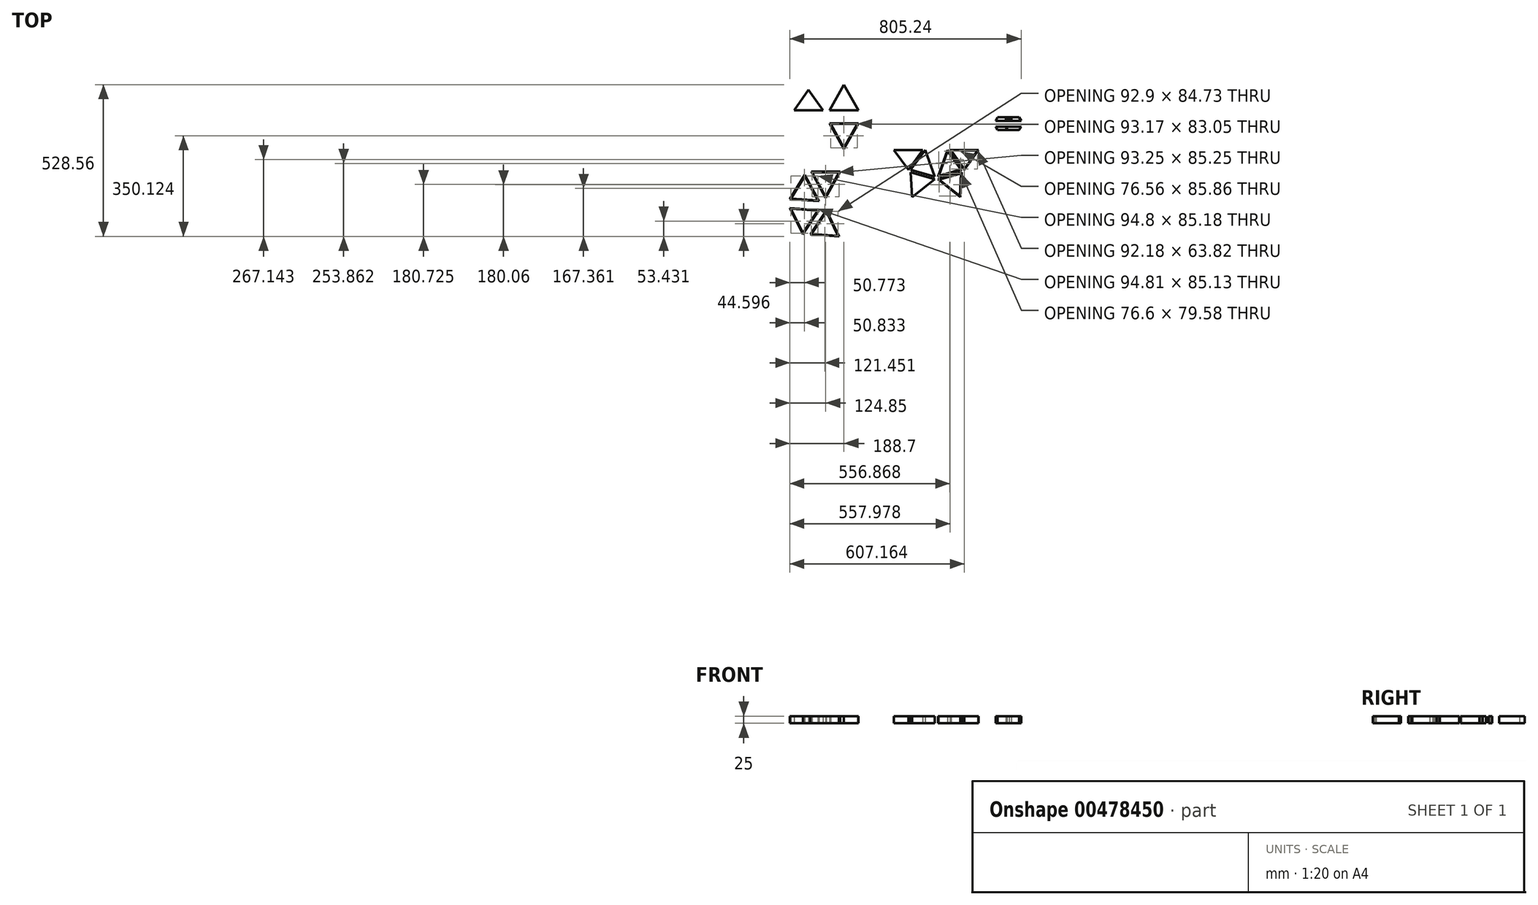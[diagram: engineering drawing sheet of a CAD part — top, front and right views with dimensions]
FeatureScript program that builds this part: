
annotation { "Feature Type Name" : "Feature", "Feature Type Description" : "" }
export const myFeature = defineFeature(function(context is Context, id is Id, definition is map)
    precondition{}
    {
        {
            var Q0;
            Q0=qCreatedBy(makeId("Top.planeOp"),FACE);
            var sketch = newSketch(context, id + "F0", { "sketchPlane" : qUnion([Q0])});
            skLineSegment(sketch, "E0", {"start": v(-494.38, 0) * mm, "end": v(-394.38, 0) * mm});
            skLineSegment(sketch, "E1", {"start": v(-394.38, 0) * mm, "end": v(-444.38, 70.46) * mm});
            skLineSegment(sketch, "E2", {"start": v(-444.38, 70.46) * mm, "end": v(-494.38, 0) * mm});
            skLineSegment(sketch, "E3", {"start": v(-371.13, 0) * mm, "end": v(-321.13, 89.13) * mm});
            skLineSegment(sketch, "E4", {"start": v(-321.13, 89.13) * mm, "end": v(-271.13, 0) * mm});
            skLineSegment(sketch, "E5", {"start": v(-271.13, 0) * mm, "end": v(-371.13, 0) * mm});
            skLineSegment(sketch, "E6", {"start": v(-485.01, -22.9) * mm, "end": v(-304.75, -22.9) * mm, "construction": true});
            skLineSegment(sketch, "E7.MirrorCS", {"start": v(-371.13, -45.78) * mm, "end": v(-321.13, -134.92) * mm});
            skLineSegment(sketch, "E8.MirrorCS", {"start": v(-321.13, -134.92) * mm, "end": v(-271.13, -45.78) * mm});
            skLineSegment(sketch, "E9.MirrorCS", {"start": v(-271.13, -45.78) * mm, "end": v(-371.13, -45.78) * mm});
            skLineSegment(sketch, "E10.0", {"start": v(-367.71, -47.78) * mm, "end": v(-321.13, -130.83) * mm});
            skLineSegment(sketch, "E10.1", {"start": v(-274.54, -47.78) * mm, "end": v(-367.71, -47.78) * mm});
            skLineSegment(sketch, "E10.2", {"start": v(-321.13, -130.83) * mm, "end": v(-274.54, -47.78) * mm});
            skLineSegment(sketch, "E11", {"start": v(-334.98, -214.08) * mm, "end": v(-434.98, -214.08) * mm});
            skLineSegment(sketch, "E12", {"start": v(-434.98, -214.08) * mm, "end": v(-384.98, -305.5) * mm});
            skLineSegment(sketch, "E13", {"start": v(-384.98, -305.5) * mm, "end": v(-334.98, -214.08) * mm});
            skLineSegment(sketch, "E14", {"start": v(-408.08, -316.92) * mm, "end": v(-458.08, -225.5) * mm});
            skLineSegment(sketch, "E15", {"start": v(-458.08, -225.5) * mm, "end": v(-509.83, -309.66) * mm});
            skLineSegment(sketch, "E16", {"start": v(-509.83, -309.66) * mm, "end": v(-408.08, -316.92) * mm});
            skLineSegment(sketch, "E17", {"start": v(-408.08, -348.44) * mm, "end": v(-509.83, -341.19) * mm});
            skLineSegment(sketch, "E18", {"start": v(-408.08, -348.44) * mm, "end": v(-464.01, -432.54) * mm});
            skLineSegment(sketch, "E19", {"start": v(-464.01, -432.54) * mm, "end": v(-509.83, -341.19) * mm});
            skLineSegment(sketch, "E20", {"start": v(-382.47, -348.44) * mm, "end": v(-438.4, -432.54) * mm});
            skLineSegment(sketch, "E21", {"start": v(-382.47, -348.44) * mm, "end": v(-338.64, -439.43) * mm});
            skLineSegment(sketch, "E22", {"start": v(-338.64, -439.43) * mm, "end": v(-438.4, -432.54) * mm});
            skLineSegment(sketch, "E23.0", {"start": v(-411.6, -314.66) * mm, "end": v(-458.19, -229.48) * mm});
            skLineSegment(sketch, "E23.1", {"start": v(-506.4, -307.9) * mm, "end": v(-411.6, -314.66) * mm});
            skLineSegment(sketch, "E23.2", {"start": v(-458.19, -229.48) * mm, "end": v(-506.4, -307.9) * mm});
            skLineSegment(sketch, "E24.0", {"start": v(-431.6, -216.08) * mm, "end": v(-384.98, -301.33) * mm});
            skLineSegment(sketch, "E24.1", {"start": v(-338.35, -216.08) * mm, "end": v(-431.6, -216.08) * mm});
            skLineSegment(sketch, "E24.2", {"start": v(-384.98, -301.33) * mm, "end": v(-338.35, -216.08) * mm});
            skLineSegment(sketch, "E25.0", {"start": v(-463.77, -428.57) * mm, "end": v(-506.46, -343.43) * mm});
            skLineSegment(sketch, "E25.1", {"start": v(-411.65, -350.2) * mm, "end": v(-463.77, -428.57) * mm});
            skLineSegment(sketch, "E25.2", {"start": v(-411.65, -350.2) * mm, "end": v(-506.46, -343.43) * mm});
            skLineSegment(sketch, "E26.0", {"start": v(-382.75, -352.47) * mm, "end": v(-341.93, -437.2) * mm});
            skLineSegment(sketch, "E26.1", {"start": v(-382.75, -352.47) * mm, "end": v(-434.83, -430.78) * mm});
            skLineSegment(sketch, "E26.2", {"start": v(-341.93, -437.2) * mm, "end": v(-434.83, -430.78) * mm});
            skLineSegment(sketch, "E27", {"start": v(-147.33, -138.38) * mm, "end": v(-47.33, -138.38) * mm});
            skLineSegment(sketch, "E28", {"start": v(-47.33, -138.38) * mm, "end": v(-97.33, -207.61) * mm});
            skLineSegment(sketch, "E29", {"start": v(-97.33, -207.61) * mm, "end": v(-147.33, -138.38) * mm});
            skLineSegment(sketch, "E30", {"start": v(-88.6, -207.61) * mm, "end": v(-38.6, -138.38) * mm});
            skLineSegment(sketch, "E31", {"start": v(-38.6, -138.38) * mm, "end": v(-5.57, -231.5) * mm});
            skLineSegment(sketch, "E32", {"start": v(-5.57, -231.5) * mm, "end": v(-88.6, -207.61) * mm});
            skLineSegment(sketch, "E33", {"start": v(-88.6, -216.88) * mm, "end": v(-5.57, -240.76) * mm});
            skLineSegment(sketch, "E34", {"start": v(-5.57, -240.76) * mm, "end": v(-83.73, -303.14) * mm});
            skLineSegment(sketch, "E35", {"start": v(-83.73, -303.14) * mm, "end": v(-88.6, -216.88) * mm});
            skLineSegment(sketch, "E36", {"start": v(0, -148.36) * mm, "end": v(0, -299.14) * mm, "construction": true});
            skLineSegment(sketch, "E37.MirrorCS", {"start": v(5.57, -231.5) * mm, "end": v(88.6, -207.61) * mm});
            skLineSegment(sketch, "E38.MirrorCS", {"start": v(47.33, -138.38) * mm, "end": v(97.33, -207.61) * mm});
            skLineSegment(sketch, "E39.MirrorCS", {"start": v(38.6, -138.38) * mm, "end": v(5.57, -231.5) * mm});
            skLineSegment(sketch, "E40.MirrorCS", {"start": v(88.6, -207.61) * mm, "end": v(38.6, -138.38) * mm});
            skLineSegment(sketch, "E41.MirrorCS", {"start": v(5.57, -240.76) * mm, "end": v(83.73, -303.14) * mm});
            skLineSegment(sketch, "E42.MirrorCS", {"start": v(83.73, -303.14) * mm, "end": v(88.6, -216.88) * mm});
            skLineSegment(sketch, "E43.MirrorCS", {"start": v(147.33, -138.38) * mm, "end": v(47.33, -138.38) * mm});
            skLineSegment(sketch, "E44.MirrorCS", {"start": v(88.6, -216.88) * mm, "end": v(5.57, -240.76) * mm});
            skLineSegment(sketch, "E45.MirrorCS", {"start": v(97.33, -207.61) * mm, "end": v(147.33, -138.38) * mm});
            skLineSegment(sketch, "E46.0", {"start": v(85.32, -206.48) * mm, "end": v(39.22, -142.64) * mm});
            skLineSegment(sketch, "E46.1", {"start": v(8.76, -228.5) * mm, "end": v(85.32, -206.48) * mm});
            skLineSegment(sketch, "E46.2", {"start": v(39.22, -142.64) * mm, "end": v(8.76, -228.5) * mm});
            skLineSegment(sketch, "E47.0", {"start": v(51.25, -140.38) * mm, "end": v(97.33, -204.2) * mm});
            skLineSegment(sketch, "E47.1", {"start": v(143.42, -140.38) * mm, "end": v(51.25, -140.38) * mm});
            skLineSegment(sketch, "E47.2", {"start": v(97.33, -204.2) * mm, "end": v(143.42, -140.38) * mm});
            skLineSegment(sketch, "E48.0", {"start": v(86.45, -219.58) * mm, "end": v(9.85, -241.61) * mm});
            skLineSegment(sketch, "E48.1", {"start": v(81.95, -299.16) * mm, "end": v(86.45, -219.58) * mm});
            skLineSegment(sketch, "E48.2", {"start": v(9.85, -241.61) * mm, "end": v(81.95, -299.16) * mm});
            skLineSegment(sketch, "E49", {"start": v(213.49, -24.83) * mm, "end": v(288.49, -24.83) * mm});
            skLineSegment(sketch, "E50", {"start": v(295.41, -36.83) * mm, "end": v(288.49, -24.83) * mm});
            skLineSegment(sketch, "E51", {"start": v(295.41, -36.83) * mm, "end": v(206.56, -36.83) * mm});
            skLineSegment(sketch, "E52", {"start": v(213.49, -24.83) * mm, "end": v(206.56, -36.83) * mm});
            skLineSegment(sketch, "E53", {"start": v(250.99, -24.83) * mm, "end": v(250.99, 154.47) * mm, "construction": true});
            skLineSegment(sketch, "E54", {"start": v(250.99, -36.83) * mm, "end": v(250.99, -24.83) * mm, "construction": true});
            skArc(sketch, "E55", {"start": v(253.9, -33.06) * mm, "mid": v(261.7, -30.6) * mm, "end": v(253.8, -28.56) * mm});
            skPoint(sketch, "E55.centerSnap0", {"position": v(250.99, -30.83) * mm});
            skArc(sketch, "E56", {"start": v(244.6, -28.47) * mm, "mid": v(242.27, -30.64) * mm, "end": v(244.44, -32.96) * mm});
            skLineSegment(sketch, "E57", {"start": v(244.52, -30.72) * mm, "end": v(250.99, 154.47) * mm, "construction": true});
            skLineSegment(sketch, "E58", {"start": v(257.45, -30.72) * mm, "end": v(250.99, 154.47) * mm, "construction": true});
            skArc(sketch, "E59", {"start": v(257.45, -30.72) * mm, "mid": v(250.99, -30.83) * mm, "end": v(244.52, -30.72) * mm, "construction": true});
            skArc(sketch, "E60", {"start": v(244.44, -32.96) * mm, "mid": v(249.17, -33.07) * mm, "end": v(253.9, -33.06) * mm});
            skArc(sketch, "E61", {"start": v(244.6, -28.47) * mm, "mid": v(249.2, -28.57) * mm, "end": v(253.8, -28.56) * mm});
            skLineSegment(sketch, "E62", {"start": v(206.56, -46.86) * mm, "end": v(295.41, -46.86) * mm, "construction": true});
            skLineSegment(sketch, "E63.MirrorCS", {"start": v(295.41, -56.9) * mm, "end": v(206.56, -56.9) * mm});
            skLineSegment(sketch, "E64.MirrorCS", {"start": v(213.49, -68.9) * mm, "end": v(206.56, -56.9) * mm});
            skLineSegment(sketch, "E65.MirrorCS", {"start": v(213.49, -68.9) * mm, "end": v(288.49, -68.9) * mm});
            skLineSegment(sketch, "E66.MirrorCS", {"start": v(295.41, -56.9) * mm, "end": v(288.49, -68.9) * mm});
            skArc(sketch, "E67.MirrorCS", {"start": v(244.6, -65.26) * mm, "mid": v(242.27, -63.09) * mm, "end": v(244.44, -60.76) * mm, "construction": true});
            skCircle(sketch, "E68", {"center": v(244.52, -63) * mm, "radius": 1.5 * mm});
            skLineSegment(sketch, "E69", {"start": v(-421.9, -220.6) * mm, "end": v(-384.4, -289.17) * mm});
            skLineSegment(sketch, "E70", {"start": v(-384.4, -289.17) * mm, "end": v(-346.9, -220.6) * mm});
            skLineSegment(sketch, "E71", {"start": v(-346.9, -220.6) * mm, "end": v(-421.9, -220.6) * mm});
            skLineSegment(sketch, "E72.0", {"start": v(-418.52, -222.6) * mm, "end": v(-384.4, -285) * mm});
            skLineSegment(sketch, "E72.1", {"start": v(-350.26, -222.6) * mm, "end": v(-418.52, -222.6) * mm});
            skLineSegment(sketch, "E72.2", {"start": v(-384.4, -285) * mm, "end": v(-350.26, -222.6) * mm});
            skLineSegment(sketch, "E73.0", {"start": v(-359.4, -228.02) * mm, "end": v(-409.4, -228.02) * mm});
            skLineSegment(sketch, "E73.1", {"start": v(-384.4, -273.73) * mm, "end": v(-359.4, -228.02) * mm});
            skLineSegment(sketch, "E73.2", {"start": v(-409.4, -228.02) * mm, "end": v(-384.4, -273.73) * mm});
            skSolve(sketch);
        }
        {
            var Q0;
            Q0=makeQuery(id+"F0.imprint","IMPRINT",FACE,{"disambiguationData":[TD([[makeQuery(id+"F0.imprint","IMPRINT",EDGE,{"derivedFrom":sQuery(id+"F0.wireOp",EDGE,"E0")}),1.0]])]});
            var Q1;
            Q1=makeQuery(id+"F0.imprint","IMPRINT",FACE,{"disambiguationData":[TD([[makeQuery(id+"F0.imprint","IMPRINT",EDGE,{"derivedFrom":sQuery(id+"F0.wireOp",EDGE,"E3")}),-1.0]])]});
            var Q2;
            Q2=makeQuery(id+"F0.imprint","IMPRINT",FACE,{"disambiguationData":[TD([[makeQuery(id+"F0.imprint","IMPRINT",EDGE,{"derivedFrom":sQuery(id+"F0.wireOp",EDGE,"E7.MirrorCS")}),1.0]])]});
            var Q3;
            Q3=makeQuery(id+"F0.imprint","IMPRINT",FACE,{"disambiguationData":[TD([[makeQuery(id+"F0.imprint","IMPRINT",EDGE,{"derivedFrom":sQuery(id+"F0.wireOp",EDGE,"E14")}),1.0]])]});
            var Q4;
            Q4=makeQuery(id+"F0.imprint","IMPRINT",FACE,{"disambiguationData":[TD([[makeQuery(id+"F0.imprint","IMPRINT",EDGE,{"derivedFrom":sQuery(id+"F0.wireOp",EDGE,"E11")}),1.0]])]});
            var Q5;
            Q5=makeQuery(id+"F0.imprint","IMPRINT",FACE,{"disambiguationData":[TD([[makeQuery(id+"F0.imprint","IMPRINT",EDGE,{"derivedFrom":sQuery(id+"F0.wireOp",EDGE,"E17")}),1.0]])]});
            var Q6;
            Q6=makeQuery(id+"F0.imprint","IMPRINT",FACE,{"disambiguationData":[TD([[makeQuery(id+"F0.imprint","IMPRINT",EDGE,{"derivedFrom":sQuery(id+"F0.wireOp",EDGE,"E20")}),1.0]])]});
            var Q7;
            Q7=makeQuery(id+"F0.imprint","IMPRINT",FACE,{"disambiguationData":[TD([[makeQuery(id+"F0.imprint","IMPRINT",EDGE,{"derivedFrom":sQuery(id+"F0.wireOp",EDGE,"E27")}),-1.0]])]});
            var Q8;
            Q8=makeQuery(id+"F0.imprint","IMPRINT",FACE,{"disambiguationData":[TD([[makeQuery(id+"F0.imprint","IMPRINT",EDGE,{"derivedFrom":sQuery(id+"F0.wireOp",EDGE,"E30")}),-1.0]])]});
            var Q9;
            Q9=makeQuery(id+"F0.imprint","IMPRINT",FACE,{"disambiguationData":[TD([[makeQuery(id+"F0.imprint","IMPRINT",EDGE,{"derivedFrom":sQuery(id+"F0.wireOp",EDGE,"E33")}),-1.0]])]});
            var Q10;
            Q10=makeQuery(id+"F0.imprint","IMPRINT",FACE,{"disambiguationData":[TD([[makeQuery(id+"F0.imprint","IMPRINT",EDGE,{"derivedFrom":sQuery(id+"F0.wireOp",EDGE,"E37.MirrorCS")}),1.0]])]});
            var Q11;
            Q11=makeQuery(id+"F0.imprint","IMPRINT",FACE,{"disambiguationData":[TD([[makeQuery(id+"F0.imprint","IMPRINT",EDGE,{"derivedFrom":sQuery(id+"F0.wireOp",EDGE,"E38.MirrorCS")}),1.0]])]});
            var Q12;
            Q12=makeQuery(id+"F0.imprint","IMPRINT",FACE,{"disambiguationData":[TD([[makeQuery(id+"F0.imprint","IMPRINT",EDGE,{"derivedFrom":sQuery(id+"F0.wireOp",EDGE,"E41.MirrorCS")}),1.0]])]});
            var Q13;
            Q13=makeQuery(id+"F0.imprint","IMPRINT",FACE,{"disambiguationData":[TD([[makeQuery(id+"F0.imprint","IMPRINT",EDGE,{"derivedFrom":sQuery(id+"F0.wireOp",EDGE,"E63.MirrorCS")}),1.0]])]});
            var Q14;
            Q14=makeQuery(id+"F0.imprint","IMPRINT",FACE,{"disambiguationData":[TD([[makeQuery(id+"F0.imprint","IMPRINT",EDGE,{"derivedFrom":sQuery(id+"F0.wireOp",EDGE,"E49")}),-1.0]])]});
            extrude(context, id + "F1", {"entities" : qUnion([Q0, Q1, Q2, Q3, Q4, Q5, Q6, Q7, Q8, Q9, Q10, Q11, Q12, Q13, Q14]), "depth" : 25 * mm, "offsetDistance" : 25 * mm});
        }
    });
